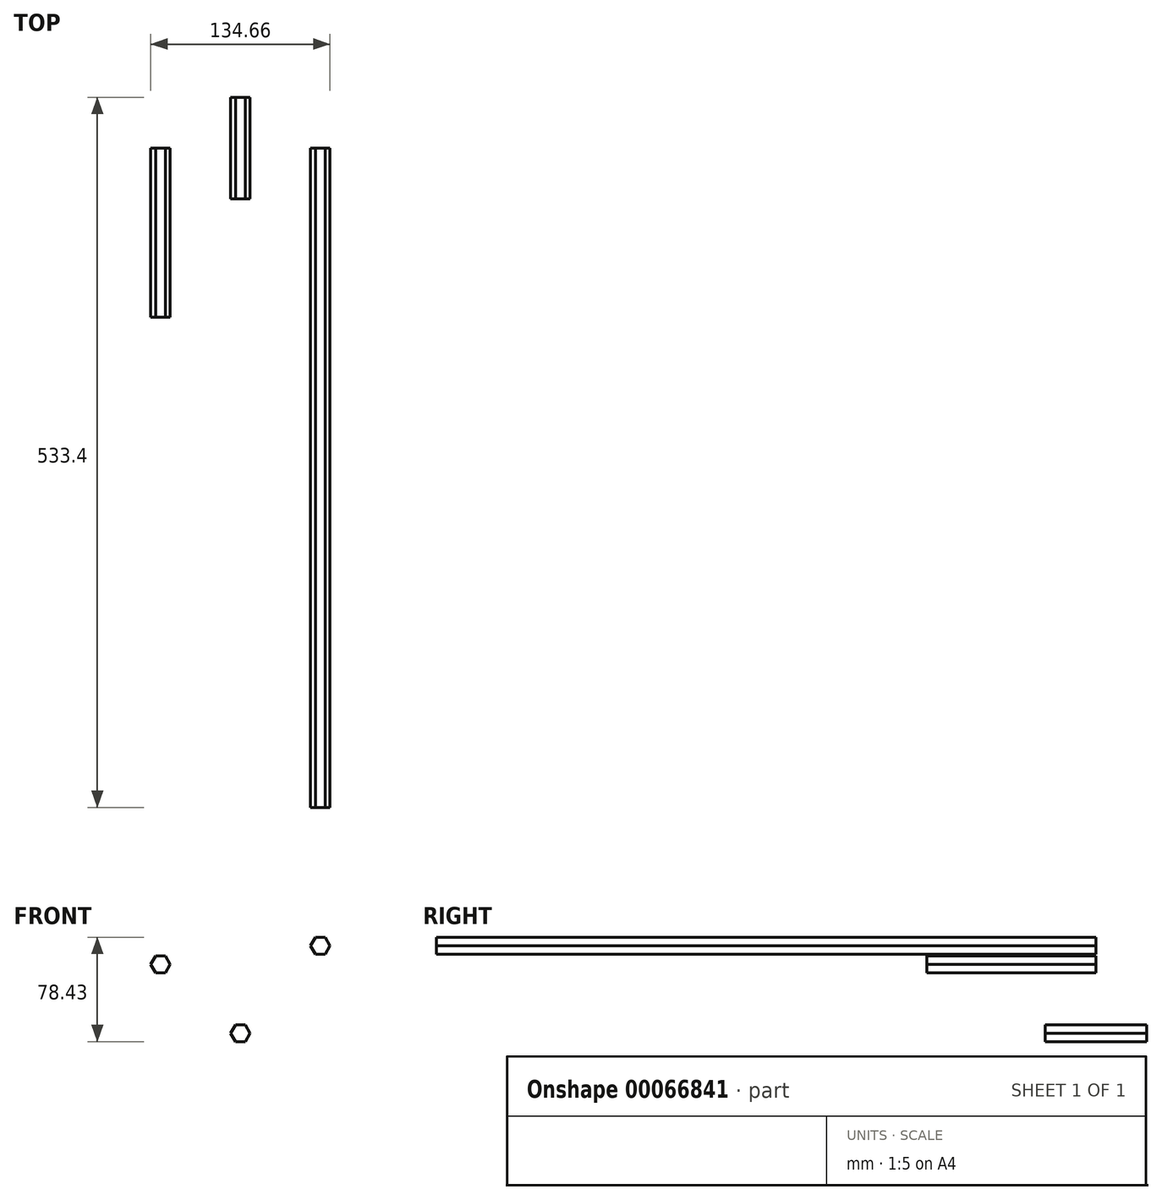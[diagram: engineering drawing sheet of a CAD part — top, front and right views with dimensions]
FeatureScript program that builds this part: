
annotation { "Feature Type Name" : "Feature", "Feature Type Description" : "" }
export const myFeature = defineFeature(function(context is Context, id is Id, definition is map)
    precondition{}
    {
        {
            var Q0;
            Q0=qCreatedBy(makeId("Front.planeOp"),FACE);
            var sketch = newSketch(context, id + "F0", { "sketchPlane" : qUnion([Q0])});
            skCircle(sketch, "E0.cCircle", {"center": v(0, 0) * mm, "radius": 6.35 * mm, "construction": true});
            skLineSegment(sketch, "E0.0", {"start": v(3.67, 6.35) * mm, "end": v(7.33, 0) * mm});
            skLineSegment(sketch, "E0.1", {"start": v(7.33, 0) * mm, "end": v(3.67, -6.35) * mm});
            skLineSegment(sketch, "E0.2", {"start": v(3.67, -6.35) * mm, "end": v(-3.67, -6.35) * mm});
            skLineSegment(sketch, "E0.3", {"start": v(-3.67, -6.35) * mm, "end": v(-7.33, 0) * mm});
            skLineSegment(sketch, "E0.4", {"start": v(-7.33, 0) * mm, "end": v(-3.67, 6.35) * mm});
            skLineSegment(sketch, "E0.5", {"start": v(-3.67, 6.35) * mm, "end": v(3.67, 6.35) * mm});
            skPoint(sketch, "E0.0.midPoint", {"position": v(5.5, 3.17) * mm});
            skCircle(sketch, "E1", {"center": v(0, 0) * mm, "radius": 7.14 * mm, "construction": true});
            skSolve(sketch);
        }
        {
            var Q0;
            Q0 = qSketchRegion(id + "F0", true);
            extrude(context, id + "F1", {"entities" : qUnion([Q0]), "depth" : 76.2 * mm, "symmetric" : true});
        }
        {
            var Q0;
            Q0=qCreatedBy(makeId("Front.planeOp"),FACE);
            var sketch = newSketch(context, id + "F2", { "sketchPlane" : qUnion([Q0])});
            skCircle(sketch, "E2.cCircle", {"center": v(-59.93, 51.75) * mm, "radius": 6.35 * mm, "construction": true});
            skLineSegment(sketch, "E2.0", {"start": v(-56.26, 58.1) * mm, "end": v(-52.6, 51.75) * mm});
            skLineSegment(sketch, "E2.1", {"start": v(-52.6, 51.75) * mm, "end": v(-56.26, 45.4) * mm});
            skLineSegment(sketch, "E2.2", {"start": v(-56.26, 45.4) * mm, "end": v(-63.6, 45.4) * mm});
            skLineSegment(sketch, "E2.3", {"start": v(-63.6, 45.4) * mm, "end": v(-67.26, 51.75) * mm});
            skLineSegment(sketch, "E2.4", {"start": v(-67.26, 51.75) * mm, "end": v(-63.6, 58.1) * mm});
            skLineSegment(sketch, "E2.5", {"start": v(-63.6, 58.1) * mm, "end": v(-56.26, 58.1) * mm});
            skPoint(sketch, "E2.0.midPoint", {"position": v(-54.43, 54.93) * mm});
            skSolve(sketch);
        }
        {
            var Q0;
            Q0=makeQuery(id+"F2.imprint","IMPRINT",FACE,{"disambiguationData":[TD([[makeQuery(id+"F2.imprint","IMPRINT",EDGE,{"derivedFrom":sQuery(id+"F2.wireOp",EDGE,"E2.0")}),-1.0]])]});
            extrude(context, id + "F3", {"entities" : qUnion([Q0]), "depth" : 127 * mm});
        }
        {
            var Q0;
            Q0=qCreatedBy(makeId("Front.planeOp"),FACE);
            var sketch = newSketch(context, id + "F4", { "sketchPlane" : qUnion([Q0])});
            skCircle(sketch, "E3.cCircle", {"center": v(60.07, 65.73) * mm, "radius": 6.35 * mm, "construction": true});
            skLineSegment(sketch, "E3.0", {"start": v(63.73, 72.08) * mm, "end": v(67.4, 65.73) * mm});
            skLineSegment(sketch, "E3.1", {"start": v(67.4, 65.73) * mm, "end": v(63.73, 59.38) * mm});
            skLineSegment(sketch, "E3.2", {"start": v(63.73, 59.38) * mm, "end": v(56.4, 59.38) * mm});
            skLineSegment(sketch, "E3.3", {"start": v(56.4, 59.38) * mm, "end": v(52.73, 65.73) * mm});
            skLineSegment(sketch, "E3.4", {"start": v(52.73, 65.73) * mm, "end": v(56.4, 72.08) * mm});
            skLineSegment(sketch, "E3.5", {"start": v(56.4, 72.08) * mm, "end": v(63.73, 72.08) * mm});
            skPoint(sketch, "E3.0.midPoint", {"position": v(65.57, 68.9) * mm});
            skSolve(sketch);
        }
        {
            var Q0;
            Q0=makeQuery(id+"F4.imprint","IMPRINT",FACE,{"disambiguationData":[TD([[makeQuery(id+"F4.imprint","IMPRINT",EDGE,{"derivedFrom":sQuery(id+"F4.wireOp",EDGE,"E3.0")}),-1.0]])]});
            extrude(context, id + "F5", {"entities" : qUnion([Q0]), "depth" : 495.3 * mm});
        }
    });
